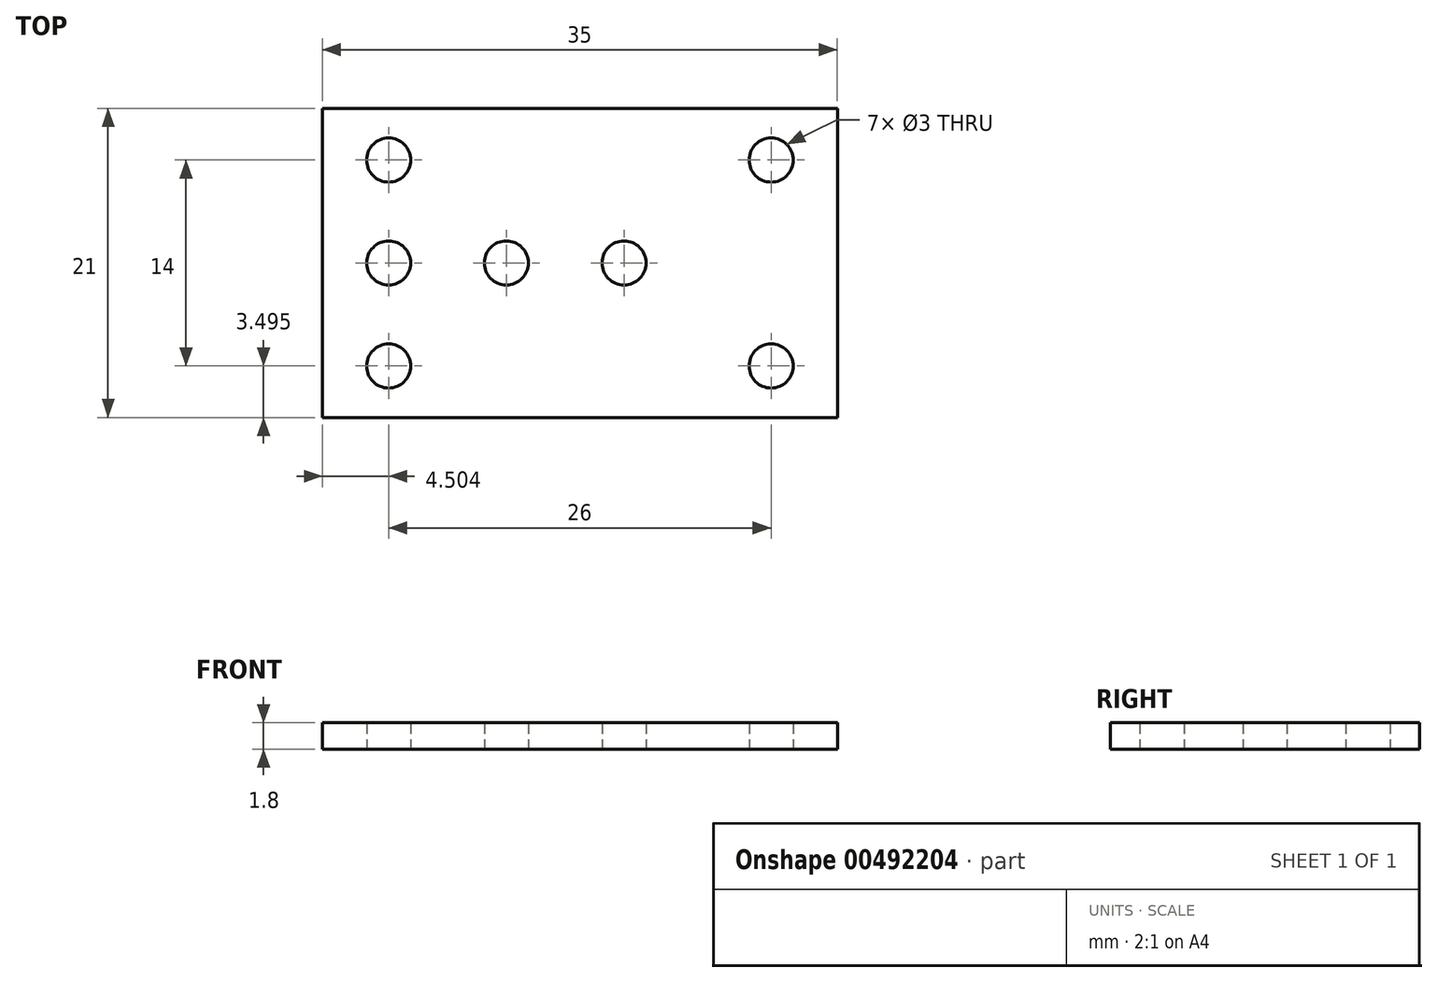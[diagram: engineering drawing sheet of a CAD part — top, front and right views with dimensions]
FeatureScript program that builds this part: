
annotation { "Feature Type Name" : "Feature", "Feature Type Description" : "" }
export const myFeature = defineFeature(function(context is Context, id is Id, definition is map)
    precondition{}
    {
        {
            var Q0;
            Q0=qCreatedBy(makeId("Top.planeOp"),FACE);
            var sketch = newSketch(context, id + "F0", { "sketchPlane" : qUnion([Q0])});
            skLineSegment(sketch, "E0.bottom", {"start": v(-9.86, 11.93) * mm, "end": v(25.14, 11.93) * mm});
            skLineSegment(sketch, "E0.top", {"start": v(-9.86, -9.07) * mm, "end": v(25.14, -9.07) * mm});
            skLineSegment(sketch, "E0.left", {"start": v(-9.86, 11.93) * mm, "end": v(-9.86, -9.07) * mm});
            skLineSegment(sketch, "E0.right", {"start": v(25.14, 11.93) * mm, "end": v(25.14, -9.07) * mm});
            skCircle(sketch, "E1", {"center": v(-5.36, 8.43) * mm, "radius": 1.5 * mm});
            skCircle(sketch, "E2", {"center": v(-5.36, 1.43) * mm, "radius": 1.5 * mm});
            skCircle(sketch, "E3", {"center": v(-5.36, -5.57) * mm, "radius": 1.5 * mm});
            skCircle(sketch, "E4.MirrorC", {"center": v(20.64, -5.57) * mm, "radius": 1.5 * mm});
            skCircle(sketch, "E5.MirrorC", {"center": v(20.64, 8.43) * mm, "radius": 1.5 * mm});
            skCircle(sketch, "E6.1.0.0", {"center": v(2.64, 1.43) * mm, "radius": 1.5 * mm});
            skCircle(sketch, "E6.2.0.0", {"center": v(10.64, 1.43) * mm, "radius": 1.5 * mm});
            skLineSegment(sketch, "E6.direction1", {"start": v(-5.36, 1.43) * mm, "end": v(2.64, 1.43) * mm, "construction": true});
            skSolve(sketch);
        }
        {
            var Q0;
            Q0=makeQuery(id+"F0.imprint","IMPRINT",FACE,{"disambiguationData":[TD([[makeQuery(id+"F0.imprint","IMPRINT",EDGE,{"derivedFrom":sQuery(id+"F0.wireOp",EDGE,"E0.bottom")}),-1.0]])]});
            extrude(context, id + "F1", {"entities" : qUnion([Q0]), "depth" : 1.8 * mm, "offsetDistance" : 25 * mm});
        }
    });
